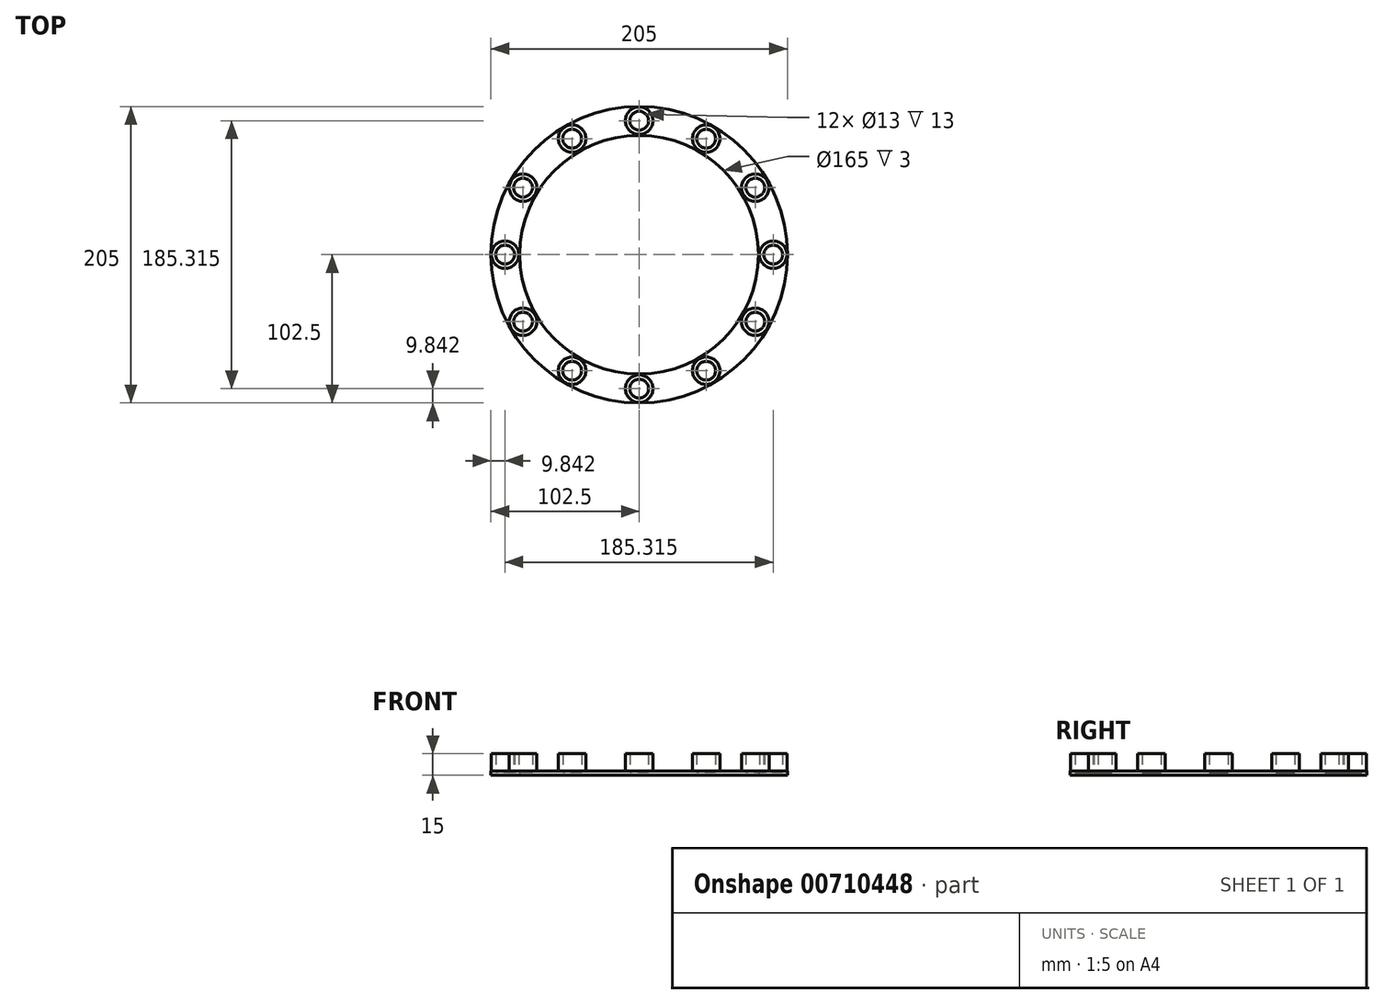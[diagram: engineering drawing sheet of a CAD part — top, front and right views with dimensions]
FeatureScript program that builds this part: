
annotation { "Feature Type Name" : "Feature", "Feature Type Description" : "" }
export const myFeature = defineFeature(function(context is Context, id is Id, definition is map)
    precondition{}
    {
        {
            var Q0;
            Q0=qCreatedBy(makeId("Top.planeOp"),FACE);
            var sketch = newSketch(context, id + "F0", { "sketchPlane" : qUnion([Q0])});
            skCircle(sketch, "E0", {"center": v(0, 0) * mm, "radius": 82.5 * mm});
            skCircle(sketch, "E1.0", {"center": v(0, 0) * mm, "radius": 102.5 * mm});
            skCircle(sketch, "E2", {"center": v(0, 92.66) * mm, "radius": 6.5 * mm});
            skCircle(sketch, "E3.0", {"center": v(0, 92.66) * mm, "radius": 9.5 * mm});
            skCircle(sketch, "E4.1.0", {"center": v(-46.33, 80.24) * mm, "radius": 9.5 * mm});
            skCircle(sketch, "E4.1.1", {"center": v(-46.33, 80.24) * mm, "radius": 6.5 * mm});
            skCircle(sketch, "E4.2.0", {"center": v(-80.24, 46.33) * mm, "radius": 9.5 * mm});
            skCircle(sketch, "E4.2.1", {"center": v(-80.24, 46.33) * mm, "radius": 6.5 * mm});
            skCircle(sketch, "E4.3.0", {"center": v(-92.66, 0) * mm, "radius": 9.5 * mm});
            skCircle(sketch, "E4.3.1", {"center": v(-92.66, 0) * mm, "radius": 6.5 * mm});
            skCircle(sketch, "E4.4.0", {"center": v(-80.24, -46.33) * mm, "radius": 9.5 * mm});
            skCircle(sketch, "E4.4.1", {"center": v(-80.24, -46.33) * mm, "radius": 6.5 * mm});
            skCircle(sketch, "E4.5.0", {"center": v(-46.33, -80.24) * mm, "radius": 9.5 * mm});
            skCircle(sketch, "E4.5.1", {"center": v(-46.33, -80.24) * mm, "radius": 6.5 * mm});
            skCircle(sketch, "E4.6.0", {"center": v(0, -92.66) * mm, "radius": 9.5 * mm});
            skCircle(sketch, "E4.6.1", {"center": v(0, -92.66) * mm, "radius": 6.5 * mm});
            skCircle(sketch, "E4.7.0", {"center": v(46.33, -80.24) * mm, "radius": 9.5 * mm});
            skCircle(sketch, "E4.7.1", {"center": v(46.33, -80.24) * mm, "radius": 6.5 * mm});
            skCircle(sketch, "E4.8.0", {"center": v(80.24, -46.33) * mm, "radius": 9.5 * mm});
            skCircle(sketch, "E4.8.1", {"center": v(80.24, -46.33) * mm, "radius": 6.5 * mm});
            skCircle(sketch, "E4.9.0", {"center": v(92.66, 0) * mm, "radius": 9.5 * mm});
            skCircle(sketch, "E4.9.1", {"center": v(92.66, 0) * mm, "radius": 6.5 * mm});
            skCircle(sketch, "E5.1.10.0", {"center": v(80.24, 46.33) * mm, "radius": 9.5 * mm});
            skCircle(sketch, "E5.2.10.0", {"center": v(80.24, 46.33) * mm, "radius": 6.5 * mm});
            skCircle(sketch, "E5.1.11.0", {"center": v(46.33, 80.24) * mm, "radius": 9.5 * mm});
            skCircle(sketch, "E5.2.11.0", {"center": v(46.33, 80.24) * mm, "radius": 6.5 * mm});
            skSolve(sketch);
        }
        {
            var Q0;
            Q0=makeQuery(id+"F0.imprint","IMPRINT",FACE,{"disambiguationData":[TD([[makeQuery(id+"F0.imprint","IMPRINT",EDGE,{"derivedFrom":sQuery(id+"F0.wireOp",EDGE,"E0")}),-1.0]])]});
            extrude(context, id + "F1", {"entities" : qUnion([Q0]), "depth" : 3 * mm, "offsetDistance" : 25 * mm});
        }
        {
            var Q0;
            Q0=makeQuery(id+"F0.imprint","IMPRINT",FACE,{"disambiguationData":[TD([[makeQuery(id+"F0.imprint","IMPRINT",EDGE,{"derivedFrom":sQuery(id+"F0.wireOp",EDGE,"E4.2.0")}),1.0]])]});
            var Q1;
            Q1=makeQuery(id+"F0.imprint","IMPRINT",FACE,{"disambiguationData":[TD([[makeQuery(id+"F0.imprint","IMPRINT",EDGE,{"derivedFrom":sQuery(id+"F0.wireOp",EDGE,"E4.1.0")}),1.0]])]});
            var Q2;
            Q2=makeQuery(id+"F0.imprint","IMPRINT",FACE,{"disambiguationData":[TD([[makeQuery(id+"F0.imprint","IMPRINT",EDGE,{"derivedFrom":sQuery(id+"F0.wireOp",EDGE,"E2")}),-1.0]])]});
            var Q3;
            Q3=makeQuery(id+"F0.imprint","IMPRINT",FACE,{"disambiguationData":[TD([[makeQuery(id+"F0.imprint","IMPRINT",EDGE,{"derivedFrom":sQuery(id+"F0.wireOp",EDGE,"E4.9.0")}),1.0]])]});
            var Q4;
            Q4=makeQuery(id+"F0.imprint","IMPRINT",FACE,{"disambiguationData":[TD([[makeQuery(id+"F0.imprint","IMPRINT",EDGE,{"derivedFrom":sQuery(id+"F0.wireOp",EDGE,"E4.8.0")}),1.0]])]});
            var Q5;
            Q5=makeQuery(id+"F0.imprint","IMPRINT",FACE,{"disambiguationData":[TD([[makeQuery(id+"F0.imprint","IMPRINT",EDGE,{"derivedFrom":sQuery(id+"F0.wireOp",EDGE,"E4.7.0")}),1.0]])]});
            var Q6;
            Q6=makeQuery(id+"F0.imprint","IMPRINT",FACE,{"disambiguationData":[TD([[makeQuery(id+"F0.imprint","IMPRINT",EDGE,{"derivedFrom":sQuery(id+"F0.wireOp",EDGE,"E4.6.0")}),1.0]])]});
            var Q7;
            Q7=makeQuery(id+"F0.imprint","IMPRINT",FACE,{"disambiguationData":[TD([[makeQuery(id+"F0.imprint","IMPRINT",EDGE,{"derivedFrom":sQuery(id+"F0.wireOp",EDGE,"E4.5.0")}),1.0]])]});
            var Q8;
            Q8=makeQuery(id+"F0.imprint","IMPRINT",FACE,{"disambiguationData":[TD([[makeQuery(id+"F0.imprint","IMPRINT",EDGE,{"derivedFrom":sQuery(id+"F0.wireOp",EDGE,"E4.4.0")}),1.0]])]});
            var Q9;
            Q9=makeQuery(id+"F0.imprint","IMPRINT",FACE,{"disambiguationData":[TD([[makeQuery(id+"F0.imprint","IMPRINT",EDGE,{"derivedFrom":sQuery(id+"F0.wireOp",EDGE,"E4.3.0")}),1.0]])]});
            var Q10;
            Q10=makeQuery(id+"F0.imprint","IMPRINT",FACE,{"disambiguationData":[TD([[makeQuery(id+"F0.imprint","IMPRINT",EDGE,{"derivedFrom":sQuery(id+"F0.wireOp",EDGE,"E5.1.11.0")}),1.0]])]});
            var Q11;
            Q11=makeQuery(id+"F0.imprint","IMPRINT",FACE,{"disambiguationData":[TD([[makeQuery(id+"F0.imprint","IMPRINT",EDGE,{"derivedFrom":sQuery(id+"F0.wireOp",EDGE,"E5.1.10.0")}),1.0]])]});
            extrude(context, id + "F2", {"entities" : qUnion([Q0, Q1, Q2, Q3, Q4, Q5, Q6, Q7, Q8, Q9, Q10, Q11]), "operationType" : NewBodyOperationType.ADD, "depth" : 15 * mm, "offsetDistance" : 25 * mm});
        }
        {
            var Q0;
            Q0=makeQuery(id+"F0.imprint","IMPRINT",FACE,{"disambiguationData":[TD([[makeQuery(id+"F0.imprint","IMPRINT",EDGE,{"derivedFrom":sQuery(id+"F0.wireOp",EDGE,"E4.1.1")}),1.0]])]});
            var Q1;
            Q1=makeQuery(id+"F0.imprint","IMPRINT",FACE,{"disambiguationData":[TD([[makeQuery(id+"F0.imprint","IMPRINT",EDGE,{"derivedFrom":sQuery(id+"F0.wireOp",EDGE,"E2")}),1.0]])]});
            var Q2;
            Q2=makeQuery(id+"F0.imprint","IMPRINT",FACE,{"disambiguationData":[TD([[makeQuery(id+"F0.imprint","IMPRINT",EDGE,{"derivedFrom":sQuery(id+"F0.wireOp",EDGE,"E4.9.1")}),1.0]])]});
            var Q3;
            Q3=makeQuery(id+"F0.imprint","IMPRINT",FACE,{"disambiguationData":[TD([[makeQuery(id+"F0.imprint","IMPRINT",EDGE,{"derivedFrom":sQuery(id+"F0.wireOp",EDGE,"E4.8.1")}),1.0]])]});
            var Q4;
            Q4=makeQuery(id+"F0.imprint","IMPRINT",FACE,{"disambiguationData":[TD([[makeQuery(id+"F0.imprint","IMPRINT",EDGE,{"derivedFrom":sQuery(id+"F0.wireOp",EDGE,"E4.7.1")}),1.0]])]});
            var Q5;
            Q5=makeQuery(id+"F0.imprint","IMPRINT",FACE,{"disambiguationData":[TD([[makeQuery(id+"F0.imprint","IMPRINT",EDGE,{"derivedFrom":sQuery(id+"F0.wireOp",EDGE,"E4.6.1")}),1.0]])]});
            var Q6;
            Q6=makeQuery(id+"F0.imprint","IMPRINT",FACE,{"disambiguationData":[TD([[makeQuery(id+"F0.imprint","IMPRINT",EDGE,{"derivedFrom":sQuery(id+"F0.wireOp",EDGE,"E4.5.1")}),1.0]])]});
            var Q7;
            Q7=makeQuery(id+"F0.imprint","IMPRINT",FACE,{"disambiguationData":[TD([[makeQuery(id+"F0.imprint","IMPRINT",EDGE,{"derivedFrom":sQuery(id+"F0.wireOp",EDGE,"E4.4.1")}),1.0]])]});
            var Q8;
            Q8=makeQuery(id+"F0.imprint","IMPRINT",FACE,{"disambiguationData":[TD([[makeQuery(id+"F0.imprint","IMPRINT",EDGE,{"derivedFrom":sQuery(id+"F0.wireOp",EDGE,"E4.3.1")}),1.0]])]});
            var Q9;
            Q9=makeQuery(id+"F0.imprint","IMPRINT",FACE,{"disambiguationData":[TD([[makeQuery(id+"F0.imprint","IMPRINT",EDGE,{"derivedFrom":sQuery(id+"F0.wireOp",EDGE,"E4.2.1")}),1.0]])]});
            var Q10;
            Q10=makeQuery(id+"F0.imprint","IMPRINT",FACE,{"disambiguationData":[TD([[makeQuery(id+"F0.imprint","IMPRINT",EDGE,{"derivedFrom":sQuery(id+"F0.wireOp",EDGE,"E5.1.11.0")}),1.0]])]});
            var Q11;
            Q11=makeQuery(id+"F0.imprint","IMPRINT",FACE,{"disambiguationData":[TD([[makeQuery(id+"F0.imprint","IMPRINT",EDGE,{"derivedFrom":sQuery(id+"F0.wireOp",EDGE,"E5.1.10.0")}),1.0]])]});
            var Q12;
            Q12=makeQuery(id+"F0.imprint","IMPRINT",FACE,{"disambiguationData":[TD([[makeQuery(id+"F0.imprint","IMPRINT",EDGE,{"derivedFrom":sQuery(id+"F0.wireOp",EDGE,"E5.2.11.0")}),1.0]])]});
            var Q13;
            Q13=makeQuery(id+"F0.imprint","IMPRINT",FACE,{"disambiguationData":[TD([[makeQuery(id+"F0.imprint","IMPRINT",EDGE,{"derivedFrom":sQuery(id+"F0.wireOp",EDGE,"E5.2.10.0")}),1.0]])]});
            extrude(context, id + "F3", {"entities" : qUnion([Q0, Q1, Q2, Q3, Q4, Q5, Q6, Q7, Q8, Q9, Q10, Q11, Q12, Q13]), "operationType" : NewBodyOperationType.ADD, "depth" : 2 * mm, "offsetDistance" : 25 * mm});
        }
    });
